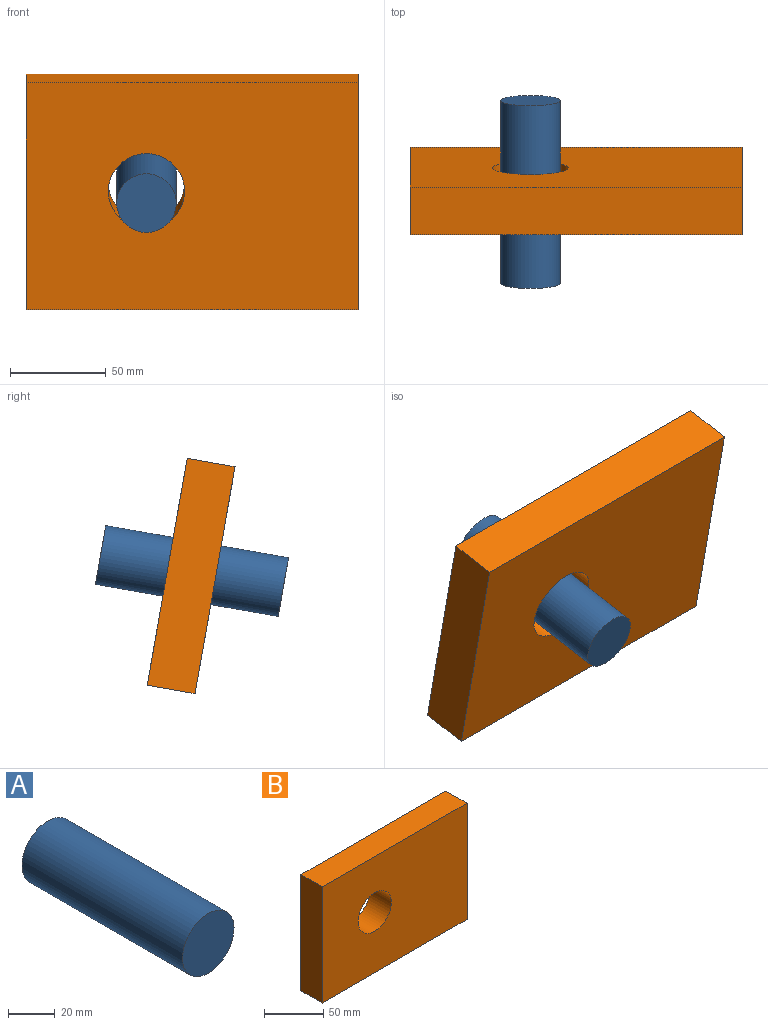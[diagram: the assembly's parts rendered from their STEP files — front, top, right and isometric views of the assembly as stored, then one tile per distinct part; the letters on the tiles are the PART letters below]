
ASSEMBLY  parts=2 mates=1
PART A: 3 faces, bbox 31.2x97x31.2 mm
  f0: cylinder r=15.58mm len=97.03mm, axis (0,1,0), area 9499.3mm2, adj f1,f2
  f1: plane 31.16x31.16mm, normal (0,-1,0), area 762.7mm2, adj f0
  f2: plane 31.16x31.16mm, normal (0,1,0), area 762.7mm2, adj f0
PART B: 7 faces, bbox 173.6x25.4x120.5 mm
  f0: plane 173.64x25.4mm, normal (0,0,1), area 4410.4mm2, adj f1,f4,f5,f6
  f1: plane 120.48x25.4mm, normal (-1,0,0), area 3060.3mm2, adj f0,f2,f5,f6
  f2: plane 173.64x25.4mm, normal (0,0,-1), area 4410.4mm2, adj f1,f4,f5,f6
  f3: cylinder r=19.96mm len=39.92mm, axis (0,1,0), area 3185.9mm2, adj f5,f6
  f4: plane 120.48x25.4mm, normal (1,0,0), area 3060.3mm2, adj f0,f2,f5,f6
  f5: plane 173.64x120.48mm, normal (0,-1,0), area 19668.7mm2, adj f0,f1,f2,f3,f4
  f6: plane 173.64x120.48mm, normal (0,1,0), area 19668.7mm2, adj f0,f1,f2,f3,f4
PLACE A rot(axis=(1,0,0),10deg) t=(-40.19,66.85,-9.8)mm
PLACE B rot(axis=(1,0,0),10deg) t=(-40.19,31.58,-16.02)mm
MATE fastened B.f3 <-> A.f0  axis (0,0.98,0.17) through (-40.19,19.07,-18.23)mm
